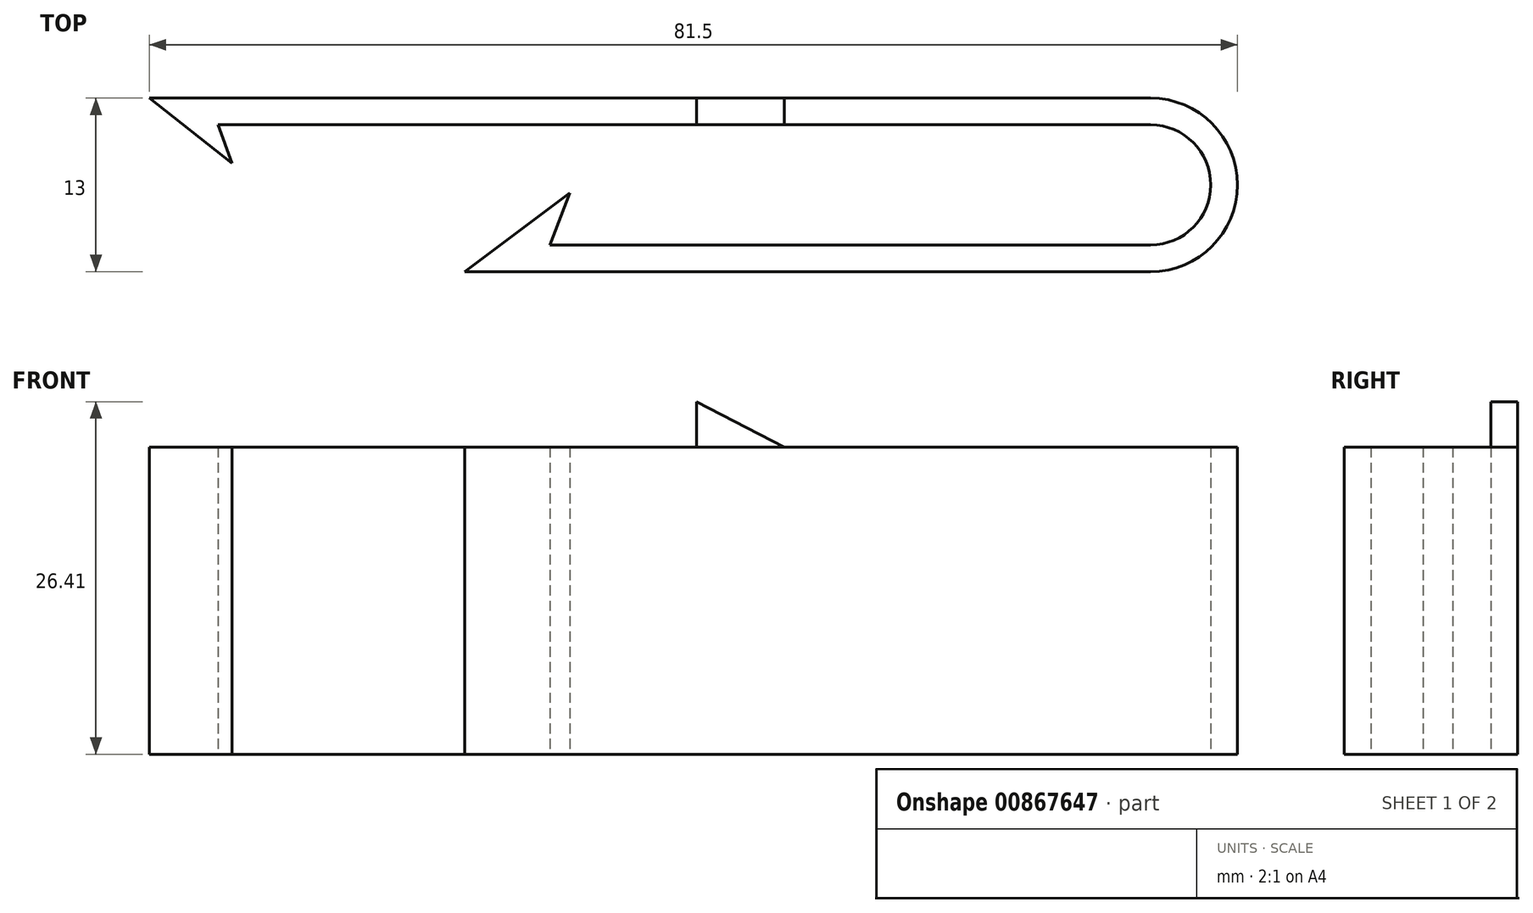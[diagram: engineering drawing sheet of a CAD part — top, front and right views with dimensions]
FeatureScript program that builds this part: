
annotation { "Feature Type Name" : "Feature", "Feature Type Description" : "" }
export const myFeature = defineFeature(function(context is Context, id is Id, definition is map)
    precondition{}
    {
        {
            var Q0;
            Q0=qCreatedBy(makeId("Top.planeOp"),FACE);
            var sketch = newSketch(context, id + "F0", { "sketchPlane" : qUnion([Q0])});
            skLineSegment(sketch, "E0", {"start": v(-47.55, 18.97) * mm, "end": v(22.31, 18.97) * mm});
            skLineSegment(sketch, "E1", {"start": v(22.31, 9.97) * mm, "end": v(-22.69, 9.97) * mm});
            skArc(sketch, "E2", {"start": v(22.31, 9.97) * mm, "mid": v(26.81, 14.47) * mm, "end": v(22.31, 18.97) * mm});
            skLineSegment(sketch, "E3.0", {"start": v(22.31, 7.97) * mm, "end": v(-29.06, 7.97) * mm});
            skArc(sketch, "E3.1", {"start": v(22.31, 7.97) * mm, "mid": v(28.81, 14.47) * mm, "end": v(22.31, 20.97) * mm});
            skLineSegment(sketch, "E3.2", {"start": v(-52.69, 20.97) * mm, "end": v(22.31, 20.97) * mm});
            skLineSegment(sketch, "E4", {"start": v(-47.55, 18.97) * mm, "end": v(-46.5, 16.1) * mm});
            skLineSegment(sketch, "E5", {"start": v(-46.5, 16.1) * mm, "end": v(-52.69, 20.97) * mm});
            skLineSegment(sketch, "E6", {"start": v(-22.69, 9.97) * mm, "end": v(-21.2, 13.88) * mm});
            skLineSegment(sketch, "E7", {"start": v(-21.2, 13.88) * mm, "end": v(-29.06, 7.97) * mm});
            skSolve(sketch);
        }
        {
            var Q0;
            Q0=makeQuery(id+"F0.imprint","IMPRINT",FACE,{"disambiguationData":[TD([[makeQuery(id+"F0.imprint","IMPRINT",EDGE,{"derivedFrom":sQuery(id+"F0.wireOp",EDGE,"E0")}),1.0]])]});
            extrude(context, id + "F1", {"entities" : qUnion([Q0]), "depth" : 23 * mm, "offsetDistance" : 25 * mm});
        }
        {
            var Q0;
            Q0=makeQuery(id+"F1.opExtrude","SWEPT_FACE",FACE,{"disambiguationData":[OSD([sQuery(id+"F0.wireOp",EDGE,"E3.2")])]});
            var sketch = newSketch(context, id + "F2", { "sketchPlane" : qUnion([Q0])});
            skLineSegment(sketch, "E8", {"start": v(11.69, 23) * mm, "end": v(11.69, 26.41) * mm});
            skLineSegment(sketch, "E9", {"start": v(11.69, 26.41) * mm, "end": v(5.13, 23) * mm});
            skLineSegment(sketch, "E10", {"start": v(5.13, 23) * mm, "end": v(11.69, 23) * mm});
            skSolve(sketch);
        }
        {
            var Q0;
            Q0=makeQuery(id+"F2.imprint","IMPRINT",FACE,{"disambiguationData":[TD([[makeQuery(id+"F2.imprint","IMPRINT",EDGE,{"derivedFrom":sQuery(id+"F2.wireOp",EDGE,"E8")}),1.0]])]});
            extrude(context, id + "F3", {"entities" : qUnion([Q0]), "oppositeDirection" : true, "depth" : 2 * mm, "offsetDistance" : 25 * mm});
        }
    });
